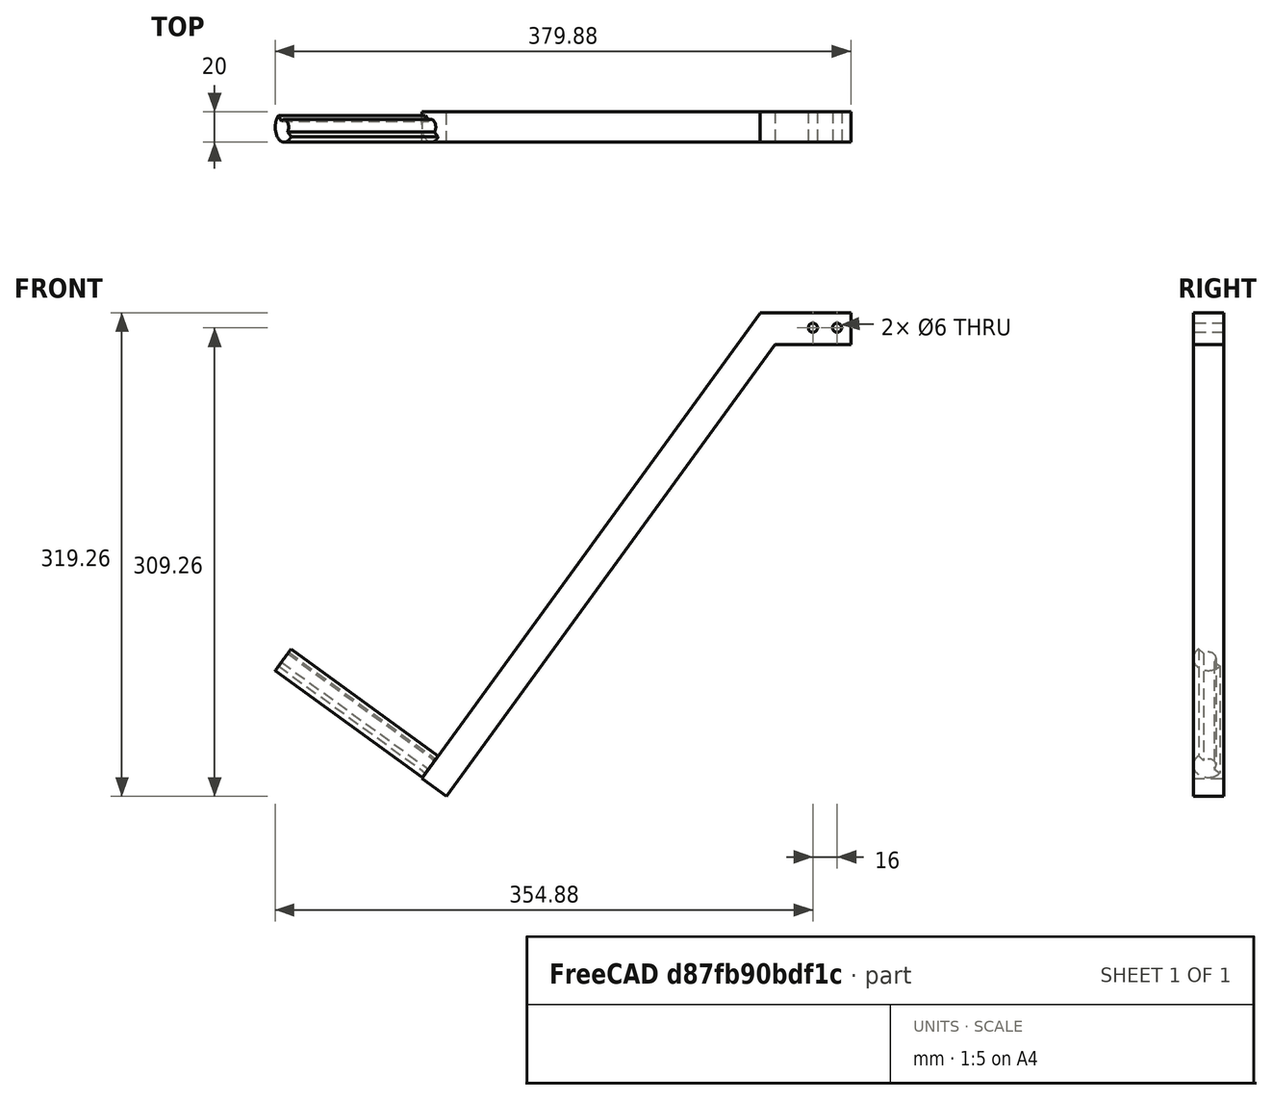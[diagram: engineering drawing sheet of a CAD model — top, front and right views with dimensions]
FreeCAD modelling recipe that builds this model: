
FCSTD DOCUMENT  (FreeCAD 0.16R6704 (Git))
Label: Soporte reposapies izquierdo
License: All rights reserved
LicenseURL: http://en.wikipedia.org/wiki/All_rights_reserved
objects: Part::Cylinder×7, Part::Cut×6, Part::Box×2, Part::MultiFuse×2
note: 17 computed .brp shape members not serialized (recipe doc carries the construction recipe); baked Part::Feature solids carry a one-line shape summary decoded from their .brp

FEATURE [Part::Box] Box086  label="Cubo060"
  Height = 380
  Length = 20
  Placement = pos=(-291,469,-86.5) rot=(0,1,0;0.628319rad)
  Width = 20
FEATURE [Part::Box] Box087  label="Cubo061"
  Height = 21
  Length = 60
  Placement = pos=(-68,469,200) rot=(0,0,1;0rad)
  Width = 20
FEATURE [Part::MultiFuse] Fusion045
  Placement = pos=(15,0,0) rot=(0,0,1;0rad)
  Shapes = -> [Box086,Box087]
FEATURE [Part::Cylinder] Cylinder263  label="Cilindro153"
  Angle = 360
  Height = 37
  Placement = pos=(-2,496,211) rot=(1,0,0;1.5708rad)
  Radius = 3
FEATURE [Part::Cut] Cut281
  Base = -> Fusion045
  Placement = pos=(-448,-479,0) rot=(0,0,1;0rad)
  Tool = -> Cylinder263
FEATURE [Part::Cylinder] Cylinder267  label="Agujero reposapies006"
  Angle = 360
  Height = 60
  Placement = pos=(-466,20,211) rot=(1,0,0;1.5708rad)
  Radius = 3
FEATURE [Part::Cut] Cut288
  Base = -> Cut281
  Tool = -> Cylinder267
FEATURE [Part::Cylinder] Cylinder273  label="Cilindro160"
  Angle = 360
  Height = 120
  Placement = pos=(-292,0,98.9) rot=(0,1,0;2.19911rad)
  Radius = 10
FEATURE [Part::Cylinder] Cylinder274  label="Cilindro161"
  Angle = 50
  Height = 130
  Placement = pos=(-292,0,98.9) rot=(0,1,0;2.19911rad)
  Radius = 11
FEATURE [Part::Cylinder] Cylinder275  label="Cilindro162"
  Angle = 360
  Height = 130
  Placement = pos=(-292,0,98.9) rot=(0,1,0;2.19911rad)
  Radius = 5
FEATURE [Part::Cut] Cut293
  Base = -> Cylinder274
  Tool = -> Cylinder275
FEATURE [Part::Cylinder] Cylinder276  label="Cilindro163"
  Angle = 220
  Height = 120
  Placement = pos=(-292,0,98.9) rot=(0,1,0;2.19911rad)
  Radius = 11
FEATURE [Part::Cylinder] Cylinder277  label="Cilindro164"
  Angle = 360
  Height = 130
  Placement = pos=(-292,0,98.9) rot=(0,1,0;2.19911rad)
  Radius = 5
FEATURE [Part::Cut] Cut294
  Base = -> Cylinder276
  Tool = -> Cylinder277
FEATURE [Part::Cut] Cut295
  Base = -> Cut294
  Tool = -> Cut293
FEATURE [Part::Cut] Cut296
  Base = -> Cylinder273
  Placement = pos=(-523,0,-106) rot=(0,0,1;0rad)
  Tool = -> Cut295
FEATURE [Part::MultiFuse] Fusion082
  Shapes = -> [Cut288,Cut296]
